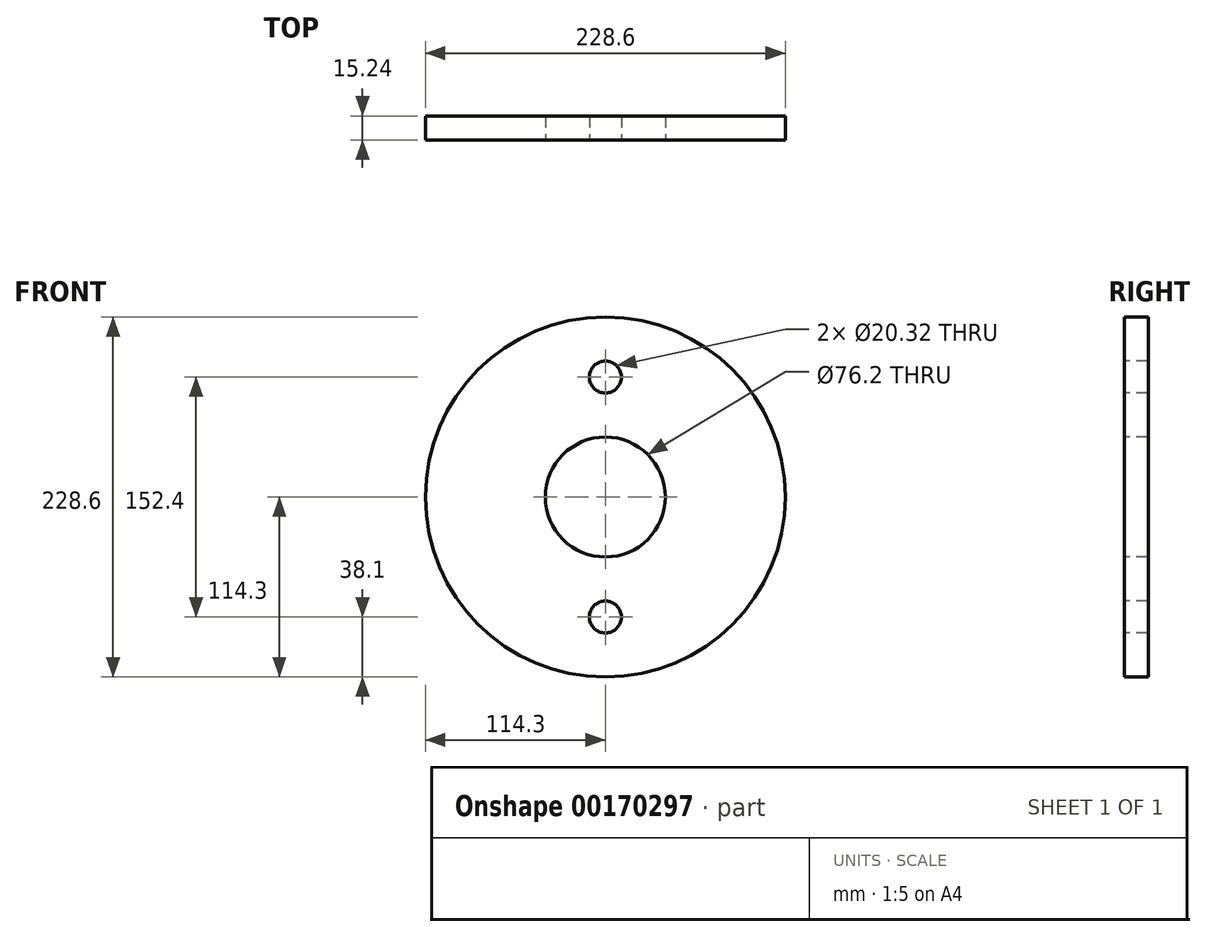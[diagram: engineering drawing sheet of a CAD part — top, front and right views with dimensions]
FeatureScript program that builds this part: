
annotation { "Feature Type Name" : "Feature", "Feature Type Description" : "" }
export const myFeature = defineFeature(function(context is Context, id is Id, definition is map)
    precondition{}
    {
        {
            var Q0;
            Q0=qCreatedBy(makeId("Front.planeOp"),FACE);
            var sketch = newSketch(context, id + "F0", { "sketchPlane" : qUnion([Q0])});
            skCircle(sketch, "E0", {"center": v(0, 0) * mm, "radius": 114.3 * mm});
            skSolve(sketch);
        }
        {
            var Q0;
            Q0=makeQuery(id+"F0.imprint","IMPRINT",FACE,{"disambiguationData":[TD([[makeQuery(id+"F0.imprint","IMPRINT",EDGE,{"derivedFrom":sQuery(id+"F0.wireOp",EDGE,"E0")}),1.0]])]});
            extrude(context, id + "F1", {"entities" : qUnion([Q0]), "depth" : 15.24 * mm});
        }
        {
            var Q0;
            Q0=makeQuery(id+"F1.opExtrude","CAP_FACE",FACE,{"disambiguationData":[OSD([sQuery(id+"F0.wireOp",EDGE,"E0")])],"isStart":false});
            var sketch = newSketch(context, id + "F2", { "sketchPlane" : qUnion([Q0])});
            skCircle(sketch, "E1", {"center": v(0, 0) * mm, "radius": 38.1 * mm});
            skSolve(sketch);
        }
        {
            var Q0;
            Q0=sQuery(id+"F2.wireOp",VERTEX,"E1.center");
            var Q1;
            Q1=makeQuery(id+"F1.opExtrude","SWEPT_BODY",BODY,{"disambiguationData":[OSD([sQuery(id+"F0.wireOp",EDGE,"E0")])]});
            hole(context, id + "F3", {"style" : HoleStyle.SIMPLE, "endStyle" : HoleEndStyle.THROUGH, "holeDiameter" : 76.2 * mm, "locations" : qUnion([Q0]), "scope" : qUnion([Q1]), "isTappedThrough" : true});
        }
        {
            var Q0;
            Q0=makeQuery(id+"F1.opExtrude","CAP_FACE",FACE,{"disambiguationData":[OSD([sQuery(id+"F0.wireOp",EDGE,"E0")])],"isStart":false});
            var sketch = newSketch(context, id + "F4", { "sketchPlane" : qUnion([Q0])});
            skCircle(sketch, "E2", {"center": v(0, 76.2) * mm, "radius": 10.16 * mm});
            skSolve(sketch);
        }
        {
            var Q0;
            Q0=sQuery(id+"F4.wireOp",VERTEX,"E2.center");
            var Q1;
            Q1=makeQuery(id+"F1.opExtrude","SWEPT_BODY",BODY,{"disambiguationData":[OSD([sQuery(id+"F0.wireOp",EDGE,"E0")])]});
            hole(context, id + "F5", {"style" : HoleStyle.SIMPLE, "endStyle" : HoleEndStyle.THROUGH, "holeDiameter" : 20.32 * mm, "locations" : qUnion([Q0]), "scope" : qUnion([Q1]), "isTappedThrough" : true});
        }
        {
            var Q0;
            Q0=makeQuery(id+"F1.opExtrude","CAP_FACE",FACE,{"disambiguationData":[OSD([sQuery(id+"F0.wireOp",EDGE,"E0")])],"isStart":false});
            var sketch = newSketch(context, id + "F6", { "sketchPlane" : qUnion([Q0])});
            skCircle(sketch, "E3", {"center": v(0, -76.2) * mm, "radius": 10.16 * mm});
            skSolve(sketch);
        }
        {
            var Q0;
            Q0=sQuery(id+"F6.wireOp",VERTEX,"E3.center");
            var Q1;
            Q1=makeQuery(id+"F1.opExtrude","SWEPT_BODY",BODY,{"disambiguationData":[OSD([sQuery(id+"F0.wireOp",EDGE,"E0")])]});
            hole(context, id + "F7", {"style" : HoleStyle.SIMPLE, "endStyle" : HoleEndStyle.THROUGH, "holeDiameter" : 20.32 * mm, "locations" : qUnion([Q0]), "scope" : qUnion([Q1]), "isTappedThrough" : true});
        }
    });
